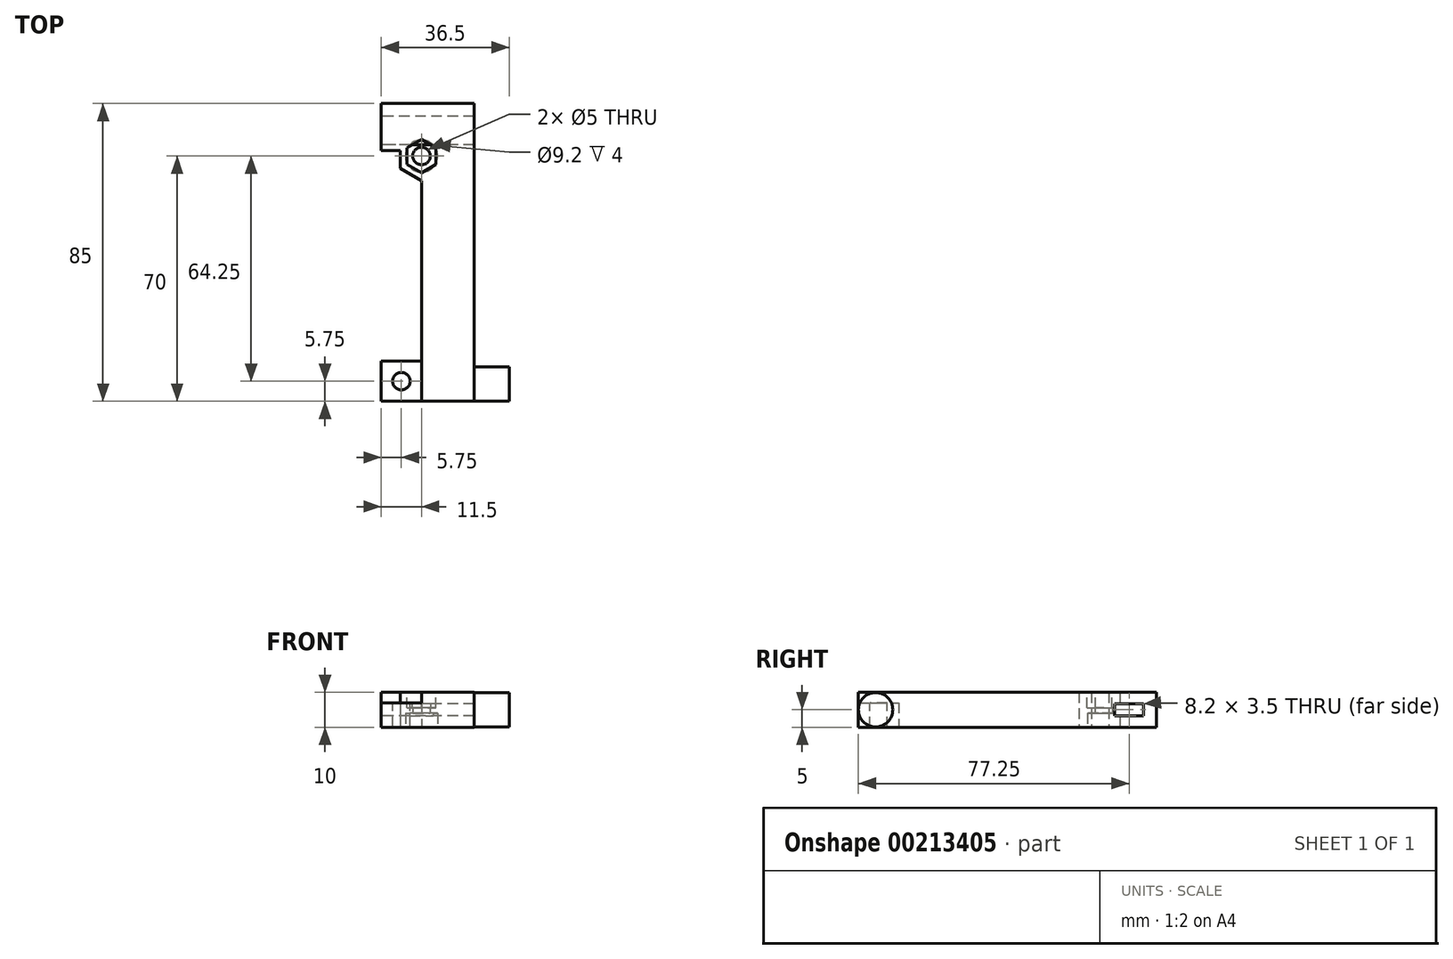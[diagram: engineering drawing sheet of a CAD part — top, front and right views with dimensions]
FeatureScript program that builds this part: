
annotation { "Feature Type Name" : "Feature", "Feature Type Description" : "" }
export const myFeature = defineFeature(function(context is Context, id is Id, definition is map)
    precondition{}
    {
        {
            var Q0;
            Q0=qCreatedBy(makeId("Top.planeOp"),FACE);
            var sketch = newSketch(context, id + "F0", { "sketchPlane" : qUnion([Q0])});
            skLineSegment(sketch, "E0.bottom", {"start": v(0, 0) * mm, "end": v(-15, 0) * mm});
            skLineSegment(sketch, "E0.top", {"start": v(0, 83) * mm, "end": v(-15, 83) * mm});
            skLineSegment(sketch, "E0.left", {"start": v(0, 0) * mm, "end": v(0, 83) * mm});
            skLineSegment(sketch, "E0.right", {"start": v(-15, 0) * mm, "end": v(-15, 83) * mm});
            skSolve(sketch);
        }
        {
            var Q0;
            Q0 = qSketchRegion(id + "F0", true);
            extrude(context, id + "F1", {"entities" : qUnion([Q0]), "depth" : 10 * mm});
        }
        {
            var Q0;
            Q0=qCreatedBy(makeId("Top.planeOp"),FACE);
            var sketch = newSketch(context, id + "F2", { "sketchPlane" : qUnion([Q0])});
            skLineSegment(sketch, "E1.bottom", {"start": v(-15, 0) * mm, "end": v(-26.5, 0) * mm});
            skLineSegment(sketch, "E1.top", {"start": v(-15, 11.5) * mm, "end": v(-26.5, 11.5) * mm});
            skLineSegment(sketch, "E1.left", {"start": v(-15, 0) * mm, "end": v(-15, 11.5) * mm});
            skLineSegment(sketch, "E1.right", {"start": v(-26.5, 0) * mm, "end": v(-26.5, 11.5) * mm});
            skSolve(sketch);
        }
        {
            var Q0;
            Q0 = qSketchRegion(id + "F2", true);
            var Q1;
            Q1=makeQuery(id+"F1.opExtrude","CAP_FACE",FACE,{"disambiguationData":[OSD([sQuery(id+"F0.wireOp",EDGE,"E0.bottom"),sQuery(id+"F0.wireOp",EDGE,"E0.top"),sQuery(id+"F0.wireOp",EDGE,"E0.left"),sQuery(id+"F0.wireOp",EDGE,"E0.right")])],"isStart":false});
            extrude(context, id + "F3", {"entities" : qUnion([Q0]), "operationType" : NewBodyOperationType.ADD, "endBound" : BoundingType.UP_TO_SURFACE, "endBoundEntityFace" : qUnion([Q1]), "depth" : 4.2 * mm});
        }
        {
            var Q0;
            Q0=qCreatedBy(makeId("Top.planeOp"),FACE);
            var sketch = newSketch(context, id + "F4", { "sketchPlane" : qUnion([Q0])});
            skLineSegment(sketch, "E2.bottom", {"start": v(-15, 83) * mm, "end": v(-26.5, 83) * mm});
            skLineSegment(sketch, "E2.top", {"start": v(-15, 71.5) * mm, "end": v(-26.5, 71.5) * mm});
            skLineSegment(sketch, "E2.left", {"start": v(-15, 83) * mm, "end": v(-15, 71.5) * mm});
            skLineSegment(sketch, "E2.right", {"start": v(-26.5, 83) * mm, "end": v(-26.5, 71.5) * mm});
            skSolve(sketch);
        }
        {
            var Q0;
            Q0 = qSketchRegion(id + "F4", true);
            var Q1;
            {var subQ0=sQuery(id+"F0.wireOp",EDGE,"E0.right");var subQ1=sQuery(id+"F0.wireOp",EDGE,"E0.left");var subQ2=sQuery(id+"F0.wireOp",EDGE,"E0.top");var subQ3=sQuery(id+"F0.wireOp",EDGE,"E0.bottom");Q1=makeQuery(id+"F3.boolean.opBoolean","MERGE",FACE,{"derivedFrom":[makeQuery(id+"F1.opExtrude","CAP_FACE",FACE,{"disambiguationData":[OSD([subQ3,subQ2,subQ1,subQ0])],"isStart":false}),makeQuery(id+"F3.opExtrude","CAP_FACE",FACE,{"disambiguationData":[OSD([subQ3,subQ2,subQ1,subQ0])],"isStart":false})]});}
            extrude(context, id + "F5", {"entities" : qUnion([Q0]), "operationType" : NewBodyOperationType.ADD, "endBound" : BoundingType.UP_TO_SURFACE, "endBoundEntityFace" : qUnion([Q1]), "depth" : 25 * mm});
        }
        {
            var Q0;
            Q0=makeQuery(id+"F5.opExtrude","SWEPT_FACE",FACE,{"disambiguationData":[OSD([sQuery(id+"F4.wireOp",EDGE,"E2.right")])]});
            var sketch = newSketch(context, id + "F6", { "sketchPlane" : qUnion([Q0])});
            skLineSegment(sketch, "E3", {"start": v(-83, 10) * mm, "end": v(-71.5, 0) * mm, "construction": true});
            skLineSegment(sketch, "E4.bottom", {"start": v(-81.35, 6.75) * mm, "end": v(-73.15, 6.75) * mm});
            skLineSegment(sketch, "E4.top", {"start": v(-81.35, 3.25) * mm, "end": v(-73.15, 3.25) * mm});
            skLineSegment(sketch, "E4.left", {"start": v(-81.35, 6.75) * mm, "end": v(-81.35, 3.25) * mm});
            skLineSegment(sketch, "E4.right", {"start": v(-73.15, 6.75) * mm, "end": v(-73.15, 3.25) * mm});
            skPoint(sketch, "E4.middle", {"position": v(-77.25, 5) * mm});
            skSolve(sketch);
        }
        {
            var Q0;
            Q0 = qSketchRegion(id + "F6", true);
            extrude(context, id + "F7", {"entities" : qUnion([Q0]), "operationType" : NewBodyOperationType.REMOVE, "endBound" : BoundingType.THROUGH_ALL, "oppositeDirection" : true, "depth" : 25 * mm});
        }
        {
            var Q0;
            Q0=qCreatedBy(makeId("Top.planeOp"),FACE);
            var sketch = newSketch(context, id + "F8", { "sketchPlane" : qUnion([Q0])});
            skCircle(sketch, "E5.cCircle", {"center": v(-15, 70) * mm, "radius": 4.1 * mm, "construction": true});
            skLineSegment(sketch, "E5.0", {"start": v(-19.1, 67.63) * mm, "end": v(-19.1, 72.37) * mm, "construction": true});
            skLineSegment(sketch, "E5.1", {"start": v(-19.1, 72.37) * mm, "end": v(-15, 74.73) * mm, "construction": true});
            skLineSegment(sketch, "E5.2", {"start": v(-15, 74.73) * mm, "end": v(-10.9, 72.37) * mm, "construction": true});
            skLineSegment(sketch, "E5.3", {"start": v(-10.9, 72.37) * mm, "end": v(-10.9, 67.63) * mm, "construction": true});
            skLineSegment(sketch, "E5.4", {"start": v(-10.9, 67.63) * mm, "end": v(-15, 65.27) * mm, "construction": true});
            skLineSegment(sketch, "E5.5", {"start": v(-15, 65.27) * mm, "end": v(-19.1, 67.63) * mm, "construction": true});
            skPoint(sketch, "E5.0.midPoint", {"position": v(-19.1, 70) * mm});
            skLineSegment(sketch, "E6", {"start": v(-15, 62.96) * mm, "end": v(-21.1, 66.48) * mm});
            skLineSegment(sketch, "E7", {"start": v(-21.1, 66.48) * mm, "end": v(-21.1, 71.5) * mm});
            skLineSegment(sketch, "E8", {"start": v(-21.1, 71.5) * mm, "end": v(-15, 71.5) * mm});
            skLineSegment(sketch, "E9", {"start": v(-15, 71.5) * mm, "end": v(-15, 62.96) * mm});
            skSolve(sketch);
        }
        {
            var Q0;
            Q0 = qSketchRegion(id + "F8", true);
            var Q1;
            {var subQ0=sQuery(id+"F0.wireOp",EDGE,"E0.right");var subQ1=sQuery(id+"F0.wireOp",EDGE,"E0.left");var subQ2=sQuery(id+"F0.wireOp",EDGE,"E0.top");var subQ3=sQuery(id+"F0.wireOp",EDGE,"E0.bottom");Q1=makeQuery(id+"F5.boolean.opBoolean","MERGE",FACE,{"derivedFrom":[makeQuery(id+"F3.boolean.opBoolean","MERGE",FACE,{"derivedFrom":[makeQuery(id+"F1.opExtrude","CAP_FACE",FACE,{"disambiguationData":[OSD([subQ3,subQ2,subQ1,subQ0])],"isStart":false}),makeQuery(id+"F3.opExtrude","CAP_FACE",FACE,{"disambiguationData":[OSD([subQ3,subQ2,subQ1,subQ0])],"isStart":false})]}),makeQuery(id+"F5.opExtrude","CAP_FACE",FACE,{"disambiguationData":[OSD([subQ3,subQ2,subQ1,subQ0])],"isStart":false})]});}
            extrude(context, id + "F9", {"entities" : qUnion([Q0]), "operationType" : NewBodyOperationType.ADD, "endBound" : BoundingType.UP_TO_SURFACE, "endBoundEntityFace" : qUnion([Q1]), "depth" : 25 * mm});
        }
        {
            var Q0;
            {var subQ0=sQuery(id+"F0.wireOp",EDGE,"E0.right");var subQ1=sQuery(id+"F0.wireOp",EDGE,"E0.left");var subQ2=sQuery(id+"F0.wireOp",EDGE,"E0.top");var subQ3=sQuery(id+"F0.wireOp",EDGE,"E0.bottom");Q0=makeQuery(id+"F9.boolean.opBoolean","MERGE",FACE,{"derivedFrom":[makeQuery(id+"F5.boolean.opBoolean","MERGE",FACE,{"derivedFrom":[makeQuery(id+"F3.boolean.opBoolean","MERGE",FACE,{"derivedFrom":[makeQuery(id+"F1.opExtrude","CAP_FACE",FACE,{"disambiguationData":[OSD([subQ3,subQ2,subQ1,subQ0])],"isStart":false}),makeQuery(id+"F3.opExtrude","CAP_FACE",FACE,{"disambiguationData":[OSD([subQ3,subQ2,subQ1,subQ0])],"isStart":false})]}),makeQuery(id+"F5.opExtrude","CAP_FACE",FACE,{"disambiguationData":[OSD([subQ3,subQ2,subQ1,subQ0])],"isStart":false})]}),makeQuery(id+"F9.opExtrude","CAP_FACE",FACE,{"disambiguationData":[OSD([subQ3,subQ2,subQ1,subQ0])],"isStart":false})]});}
            var sketch = newSketch(context, id + "F10", { "sketchPlane" : qUnion([Q0])});
            skCircle(sketch, "E10.0", {"center": v(-15, 70) * mm, "radius": 4.1 * mm, "construction": true});
            skLineSegment(sketch, "E10.1", {"start": v(-19.1, 67.63) * mm, "end": v(-19.1, 72.37) * mm});
            skLineSegment(sketch, "E10.2", {"start": v(-19.1, 72.37) * mm, "end": v(-15, 74.73) * mm});
            skLineSegment(sketch, "E10.3", {"start": v(-15, 74.73) * mm, "end": v(-10.9, 72.37) * mm});
            skLineSegment(sketch, "E10.4", {"start": v(-10.9, 72.37) * mm, "end": v(-10.9, 67.63) * mm});
            skLineSegment(sketch, "E10.5", {"start": v(-10.9, 67.63) * mm, "end": v(-15, 65.27) * mm});
            skLineSegment(sketch, "E10.6", {"start": v(-15, 65.27) * mm, "end": v(-19.1, 67.63) * mm});
            skPoint(sketch, "E10.7", {"position": v(-19.1, 70) * mm});
            skSolve(sketch);
        }
        {
            var Q0;
            Q0 = qSketchRegion(id + "F10", true);
            extrude(context, id + "F11", {"entities" : qUnion([Q0]), "operationType" : NewBodyOperationType.REMOVE, "oppositeDirection" : true, "depth" : 4.5 * mm});
        }
        {
            var Q0;
            Q0=makeQuery(id+"F9.boolean.opBoolean","MERGE",FACE,{"derivedFrom":[makeQuery(id+"F5.boolean.opBoolean","MERGE",FACE,{"derivedFrom":[makeQuery(id+"F3.boolean.opBoolean","MERGE",FACE,{"derivedFrom":[makeQuery(id+"F1.opExtrude","CAP_FACE",FACE,{"disambiguationData":[OSD([sQuery(id+"F0.wireOp",EDGE,"E0.bottom"),sQuery(id+"F0.wireOp",EDGE,"E0.top"),sQuery(id+"F0.wireOp",EDGE,"E0.left"),sQuery(id+"F0.wireOp",EDGE,"E0.right")])],"isStart":true}),makeQuery(id+"F3.opExtrude","CAP_FACE",FACE,{"disambiguationData":[OSD([sQuery(id+"F2.wireOp",EDGE,"E1.bottom"),sQuery(id+"F2.wireOp",EDGE,"E1.top"),sQuery(id+"F2.wireOp",EDGE,"E1.left"),sQuery(id+"F2.wireOp",EDGE,"E1.right")])],"isStart":true})]}),makeQuery(id+"F5.opExtrude","CAP_FACE",FACE,{"disambiguationData":[OSD([sQuery(id+"F4.wireOp",EDGE,"E2.bottom"),sQuery(id+"F4.wireOp",EDGE,"E2.top"),sQuery(id+"F4.wireOp",EDGE,"E2.left"),sQuery(id+"F4.wireOp",EDGE,"E2.right")])],"isStart":true})]}),makeQuery(id+"F9.opExtrude","CAP_FACE",FACE,{"disambiguationData":[OSD([sQuery(id+"F8.wireOp",EDGE,"c98678b9-6138-4acb-9bcd-ad9d6ded823d.0"),sQuery(id+"F8.wireOp",EDGE,"c98678b9-6138-4acb-9bcd-ad9d6ded823d.1"),sQuery(id+"F8.wireOp",EDGE,"zDzTT6Ue-StWS-4XW4-cmMm-Tmp3jdNI7cmL"),sQuery(id+"F8.wireOp",EDGE,"DZITMC2x-IZWY-Rh9R-7j46-FVzFRhCe0qYi"),sQuery(id+"F8.wireOp",EDGE,"mdpyrIY4-Xgjn-bXvS-OPaf-RnZ2SaQ3zqn2")])],"isStart":true})]});
            var sketch = newSketch(context, id + "F12", { "sketchPlane" : qUnion([Q0])});
            skCircle(sketch, "E11.0", {"center": v(-15, -70) * mm, "radius": 4.1 * mm, "construction": true});
            skLineSegment(sketch, "E11.1", {"start": v(-19.1, -67.63) * mm, "end": v(-19.1, -72.37) * mm, "construction": true});
            skLineSegment(sketch, "E11.2", {"start": v(-19.1, -72.37) * mm, "end": v(-15, -74.73) * mm, "construction": true});
            skLineSegment(sketch, "E11.3", {"start": v(-15, -74.73) * mm, "end": v(-10.9, -72.37) * mm, "construction": true});
            skLineSegment(sketch, "E11.4", {"start": v(-10.9, -72.37) * mm, "end": v(-10.9, -67.63) * mm, "construction": true});
            skLineSegment(sketch, "E11.5", {"start": v(-10.9, -67.63) * mm, "end": v(-15, -65.27) * mm, "construction": true});
            skLineSegment(sketch, "E11.6", {"start": v(-15, -65.27) * mm, "end": v(-19.1, -67.63) * mm, "construction": true});
            skPoint(sketch, "E11.7", {"position": v(-19.1, -70) * mm});
            skLineSegment(sketch, "E11.8", {"start": v(-15, -62.96) * mm, "end": v(-21.1, -66.48) * mm, "construction": true});
            skLineSegment(sketch, "E11.9", {"start": v(-21.1, -66.48) * mm, "end": v(-21.1, -71.5) * mm, "construction": true});
            skLineSegment(sketch, "E11.10", {"start": v(-21.1, -71.5) * mm, "end": v(-15, -71.5) * mm, "construction": true});
            skLineSegment(sketch, "E11.11", {"start": v(-15, -71.5) * mm, "end": v(-15, -62.96) * mm, "construction": true});
            skCircle(sketch, "E12", {"center": v(-15, -70) * mm, "radius": 4.6 * mm});
            skSolve(sketch);
        }
        {
            var Q0;
            Q0 = qSketchRegion(id + "F12", true);
            extrude(context, id + "F13", {"entities" : qUnion([Q0]), "operationType" : NewBodyOperationType.REMOVE, "oppositeDirection" : true, "depth" : 4 * mm});
        }
        {
            var Q0;
            Q0=makeQuery(id+"F13.boolean.opBoolean","COPY",FACE,{"derivedFrom":makeQuery(id+"F13.opExtrude","CAP_FACE",FACE,{"disambiguationData":[OSD([sQuery(id+"F12.wireOp",EDGE,"E12")])],"isStart":false})});
            var sketch = newSketch(context, id + "F14", { "sketchPlane" : qUnion([Q0])});
            skCircle(sketch, "E13", {"center": v(-15, -70) * mm, "radius": 2.5 * mm});
            skSolve(sketch);
        }
        {
            var Q0;
            Q0 = qSketchRegion(id + "F14", true);
            extrude(context, id + "F15", {"entities" : qUnion([Q0]), "operationType" : NewBodyOperationType.REMOVE, "endBound" : BoundingType.UP_TO_NEXT, "oppositeDirection" : true, "depth" : 25 * mm});
        }
        {
            var Q0;
            {var subQ0=sQuery(id+"F0.wireOp",EDGE,"E0.right");var subQ1=sQuery(id+"F0.wireOp",EDGE,"E0.left");var subQ2=sQuery(id+"F0.wireOp",EDGE,"E0.top");var subQ3=sQuery(id+"F0.wireOp",EDGE,"E0.bottom");Q0=makeQuery(id+"F9.boolean.opBoolean","MERGE",FACE,{"derivedFrom":[makeQuery(id+"F5.boolean.opBoolean","MERGE",FACE,{"derivedFrom":[makeQuery(id+"F3.boolean.opBoolean","MERGE",FACE,{"derivedFrom":[makeQuery(id+"F1.opExtrude","CAP_FACE",FACE,{"disambiguationData":[OSD([subQ3,subQ2,subQ1,subQ0])],"isStart":false}),makeQuery(id+"F3.opExtrude","CAP_FACE",FACE,{"disambiguationData":[OSD([subQ3,subQ2,subQ1,subQ0])],"isStart":false})]}),makeQuery(id+"F5.opExtrude","CAP_FACE",FACE,{"disambiguationData":[OSD([subQ3,subQ2,subQ1,subQ0])],"isStart":false})]}),makeQuery(id+"F9.opExtrude","CAP_FACE",FACE,{"disambiguationData":[OSD([subQ3,subQ2,subQ1,subQ0])],"isStart":false})]});}
            var sketch = newSketch(context, id + "F16", { "sketchPlane" : qUnion([Q0])});
            skLineSegment(sketch, "E14.bottom", {"start": v(-26.5, 11.5) * mm, "end": v(-15, 11.5) * mm});
            skLineSegment(sketch, "E14.top", {"start": v(-26.5, 0) * mm, "end": v(-15, 0) * mm});
            skLineSegment(sketch, "E14.left", {"start": v(-26.5, 11.5) * mm, "end": v(-26.5, 0) * mm});
            skLineSegment(sketch, "E14.right", {"start": v(-15, 11.5) * mm, "end": v(-15, 0) * mm});
            skSolve(sketch);
        }
        {
            var Q0;
            Q0 = qSketchRegion(id + "F16", true);
            extrude(context, id + "F17", {"entities" : qUnion([Q0]), "operationType" : NewBodyOperationType.REMOVE, "oppositeDirection" : true, "depth" : 3 * mm});
        }
        {
            var Q0;
            Q0=makeQuery(id+"F17.boolean.opBoolean","COPY",FACE,{"derivedFrom":makeQuery(id+"F17.opExtrude","CAP_FACE",FACE,{"disambiguationData":[OSD([sQuery(id+"F16.wireOp",EDGE,"E14.bottom"),sQuery(id+"F16.wireOp",EDGE,"E14.top"),sQuery(id+"F16.wireOp",EDGE,"E14.left"),sQuery(id+"F16.wireOp",EDGE,"E14.right")])],"isStart":false})});
            var sketch = newSketch(context, id + "F18", { "sketchPlane" : qUnion([Q0])});
            skLineSegment(sketch, "E15", {"start": v(-26.5, 11.5) * mm, "end": v(-15, 0) * mm, "construction": true});
            skCircle(sketch, "E16", {"center": v(-20.75, 5.75) * mm, "radius": 2.5 * mm});
            skSolve(sketch);
        }
        {
            var Q0;
            Q0 = qSketchRegion(id + "F18", true);
            extrude(context, id + "F19", {"entities" : qUnion([Q0]), "operationType" : NewBodyOperationType.REMOVE, "endBound" : BoundingType.UP_TO_NEXT, "oppositeDirection" : true, "depth" : 25 * mm});
        }
        {
            var Q0;
            Q0=makeQuery(id+"F1.opExtrude","SWEPT_FACE",FACE,{"disambiguationData":[OSD([sQuery(id+"F0.wireOp",EDGE,"E0.left")])]});
            var sketch = newSketch(context, id + "F20", { "sketchPlane" : qUnion([Q0])});
            skCircle(sketch, "E17", {"center": v(4.9, 5) * mm, "radius": 4.9 * mm});
            skPoint(sketch, "E17.centerSnap0", {"position": v(0, 5) * mm});
            skSolve(sketch);
        }
        {
            var Q0;
            Q0 = qSketchRegion(id + "F20", true);
            extrude(context, id + "F21", {"entities" : qUnion([Q0]), "operationType" : NewBodyOperationType.ADD, "depth" : 10 * mm});
        }
        {
            var Q0;
            Q0=qCreatedBy(makeId("Top.planeOp"),FACE);
            var sketch = newSketch(context, id + "F22", { "sketchPlane" : qUnion([Q0])});
            skLineSegment(sketch, "E18.bottom", {"start": v(0, 83) * mm, "end": v(-26.5, 83) * mm});
            skLineSegment(sketch, "E18.top", {"start": v(0, 85) * mm, "end": v(-26.5, 85) * mm});
            skLineSegment(sketch, "E18.left", {"start": v(0, 83) * mm, "end": v(0, 85) * mm});
            skLineSegment(sketch, "E18.right", {"start": v(-26.5, 83) * mm, "end": v(-26.5, 85) * mm});
            skSolve(sketch);
        }
        {
            var Q0;
            Q0 = qSketchRegion(id + "F22", true);
            var Q1;
            {var subQ0=sQuery(id+"F0.wireOp",EDGE,"E0.right");var subQ1=sQuery(id+"F0.wireOp",EDGE,"E0.left");var subQ2=sQuery(id+"F0.wireOp",EDGE,"E0.top");var subQ3=sQuery(id+"F0.wireOp",EDGE,"E0.bottom");Q1=makeQuery(id+"F9.boolean.opBoolean","MERGE",FACE,{"derivedFrom":[makeQuery(id+"F5.boolean.opBoolean","MERGE",FACE,{"derivedFrom":[makeQuery(id+"F3.boolean.opBoolean","MERGE",FACE,{"derivedFrom":[makeQuery(id+"F1.opExtrude","CAP_FACE",FACE,{"disambiguationData":[OSD([subQ3,subQ2,subQ1,subQ0])],"isStart":false}),makeQuery(id+"F3.opExtrude","CAP_FACE",FACE,{"disambiguationData":[OSD([subQ3,subQ2,subQ1,subQ0])],"isStart":false})]}),makeQuery(id+"F5.opExtrude","CAP_FACE",FACE,{"disambiguationData":[OSD([subQ3,subQ2,subQ1,subQ0])],"isStart":false})]}),makeQuery(id+"F9.opExtrude","CAP_FACE",FACE,{"disambiguationData":[OSD([subQ3,subQ2,subQ1,subQ0])],"isStart":false})]});}
            extrude(context, id + "F23", {"entities" : qUnion([Q0]), "operationType" : NewBodyOperationType.ADD, "endBound" : BoundingType.UP_TO_SURFACE, "endBoundEntityFace" : qUnion([Q1]), "depth" : 25 * mm});
        }
    });
